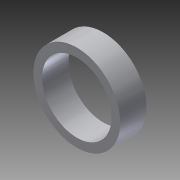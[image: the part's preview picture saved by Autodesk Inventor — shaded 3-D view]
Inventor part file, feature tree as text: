
AUTODESK INVENTOR PART (.ipt)
format: ipt  version: 2014 SP1 (Build 180222100, 222)  size: 85,504 bytes
history: native  units: in
note: dims shown in document units (in); Inventor stores cm internally (conversion verified against a paired STEP export)
features: extrude x1, sketch x1
ambient origin geometry x8: Origin, YZ Plane, XZ Plane, XY Plane, X Axis, Y Axis, Z Axis, Center Point
bodies: Solid1 (feature_tree)
feature tree (2):
  extrude  "Extrusion1"  Depth=0.19in
  sketch  "Sketch1"  dims[d0=0.5in d1=0.625in d2=0.19in d3=0.0in]
